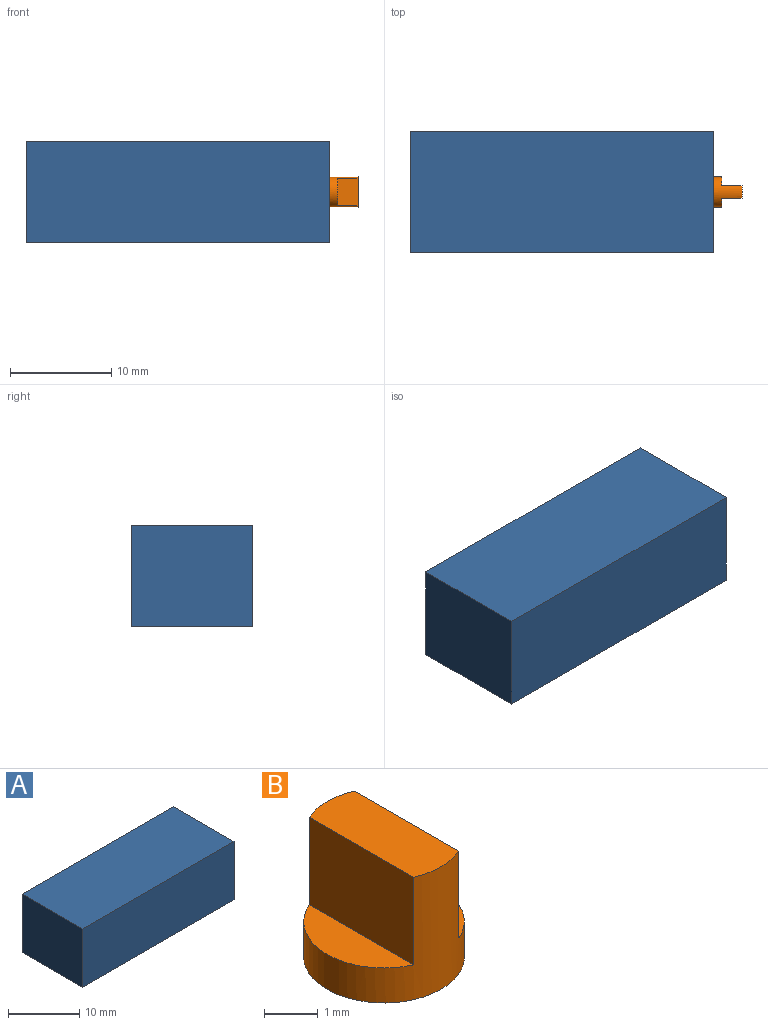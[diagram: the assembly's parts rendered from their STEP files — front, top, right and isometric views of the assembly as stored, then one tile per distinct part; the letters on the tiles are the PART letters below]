
ASSEMBLY  parts=2 mates=1
PART A: 6 faces, bbox 30x12x10 mm
  f0: plane 30x10mm, normal (0,1,0), area 300mm2, adj f1,f3,f4,f5
  f1: plane 12x10mm, normal (-1,0,0), area 120mm2, adj f0,f2,f4,f5
  f2: plane 30x10mm, normal (0,-1,0), area 300mm2, adj f1,f3,f4,f5
  f3: plane 12x10mm, normal (1,0,0), area 120mm2, adj f0,f2,f4,f5
  f4: plane 30x12mm, normal (0,0,1), area 360mm2, adj f0,f1,f2,f3
  f5: plane 30x12mm, normal (0,0,-1), area 360mm2, adj f0,f1,f2,f3
PART B: 7 faces, bbox 3x3x2.8 mm
  f0: plane 3x1.2mm, normal (0,0,1), area 3.5mm2, adj f1,f3,f5
  f1: cylinder r=1.5mm len=3mm, axis (0,0,-1), area 12.5mm2, adj f0,f2,f3,f4,f5,f6
  f2: plane 3x3mm, normal (0,0,-1), area 7.1mm2, adj f1
  f3: plane 2.75x2mm, normal (1,0,0), area 5.5mm2, adj f0,f1,f4
  f4: plane 2.75x0.9mm, normal (0,0,1), area 1.8mm2, adj f1,f3
  f5: plane 2.75x2mm, normal (-1,0,0), area 5.5mm2, adj f0,f1,f6
  f6: plane 2.75x0.9mm, normal (0,0,1), area 1.8mm2, adj f1,f5
PLACE A t=(-12.04,4.78,-4.09)mm
PLACE B rot(axis=(-0.58,0.58,-0.58),120deg) t=(22.07,4.69,0.91)mm
MATE revolute B.f1 <-> A.f3  axis (-1,0,0) through (22.07,4.69,0.91)mm
